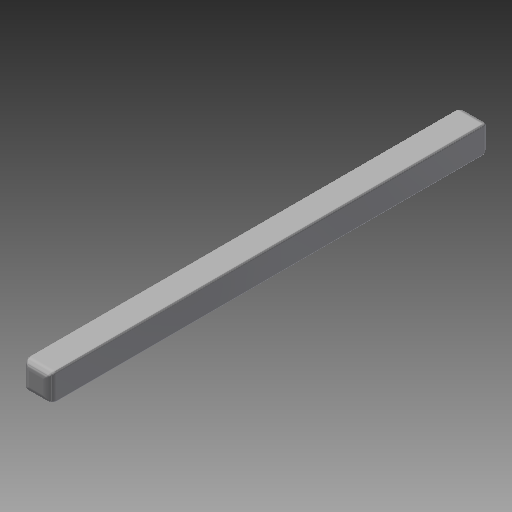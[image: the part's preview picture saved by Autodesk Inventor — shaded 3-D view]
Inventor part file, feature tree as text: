
AUTODESK INVENTOR PART (.ipt)
format: ipt  version: 2018 (Build 220112000, 112)  size: 202,752 bytes
history: native  units: mm (DEFAULTED — no unit token found)
features: plane x2, imported_body x1, other x1
ambient origin geometry x8: Origin, YZ Plane, XZ Plane, XY Plane, X Axis, Y Axis, Z Axis, Center Point
bodies: Solid1 (feature_tree)
feature tree (4):
  imported_body  "Base1"
  other  "Work Axis1"
  plane  "Work Plane1"
  plane  "Work Plane2"
